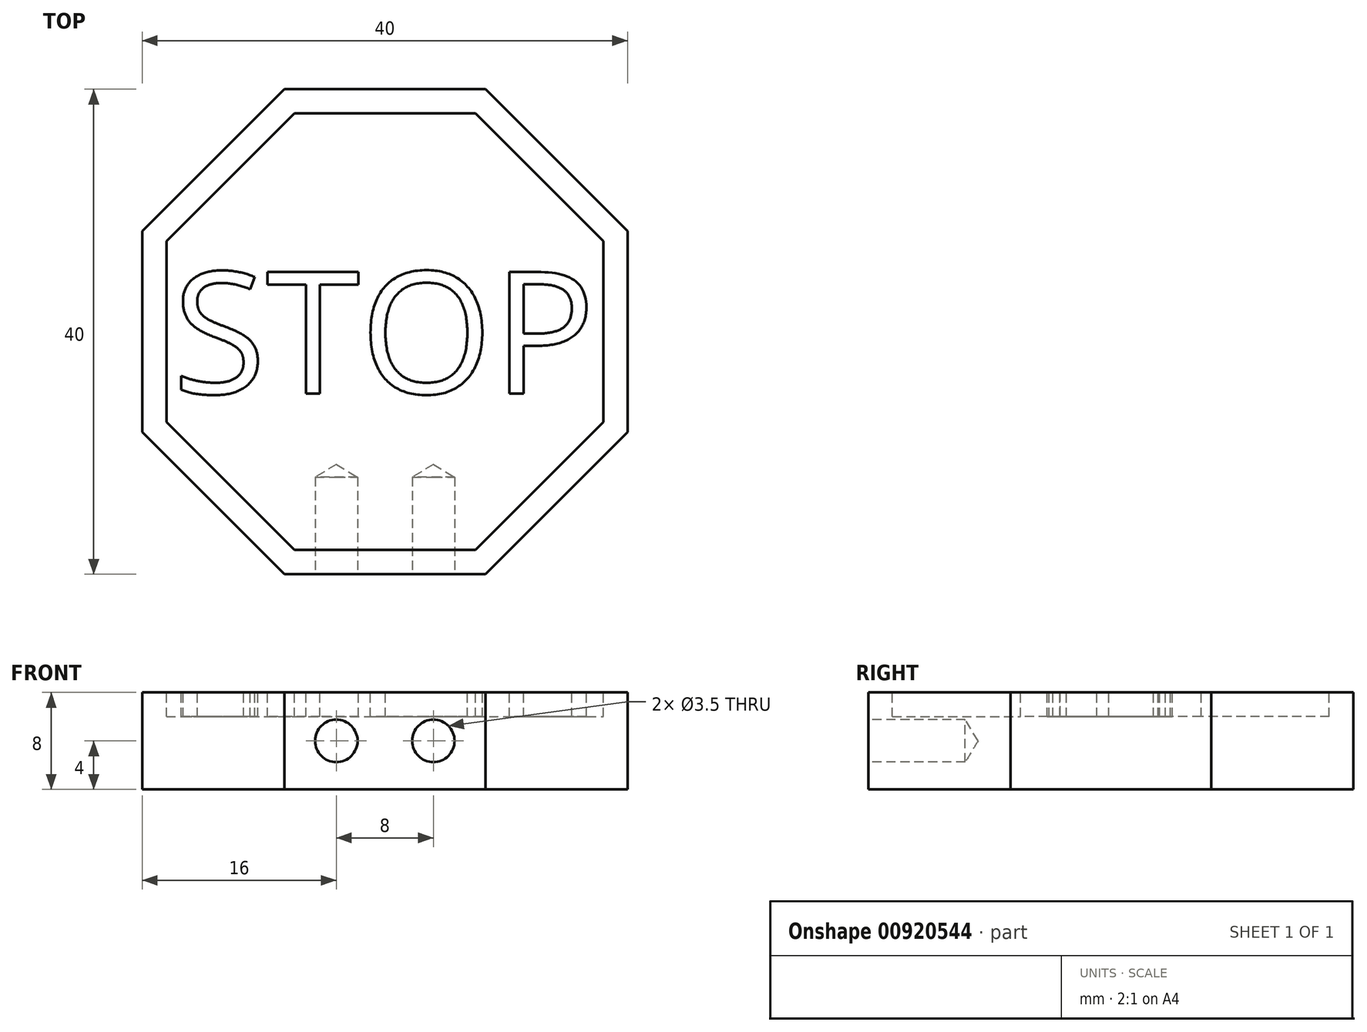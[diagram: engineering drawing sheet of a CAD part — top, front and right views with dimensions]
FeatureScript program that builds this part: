
annotation { "Feature Type Name" : "Feature", "Feature Type Description" : "" }
export const myFeature = defineFeature(function(context is Context, id is Id, definition is map)
    precondition{}
    {
        {
            var Q0;
            Q0=qCreatedBy(makeId("Top.planeOp"),FACE);
            var sketch = newSketch(context, id + "F0", { "sketchPlane" : qUnion([Q0])});
            skCircle(sketch, "E0.cCircle", {"center": v(0, 0) * mm, "radius": 20 * mm, "construction": true});
            skLineSegment(sketch, "E0.0", {"start": v(20, 8.28) * mm, "end": v(20, -8.28) * mm});
            skLineSegment(sketch, "E0.1", {"start": v(20, -8.28) * mm, "end": v(8.28, -20) * mm});
            skLineSegment(sketch, "E0.2", {"start": v(8.28, -20) * mm, "end": v(-8.28, -20) * mm});
            skLineSegment(sketch, "E0.3", {"start": v(-8.28, -20) * mm, "end": v(-20, -8.28) * mm});
            skLineSegment(sketch, "E0.4", {"start": v(-20, -8.28) * mm, "end": v(-20, 8.28) * mm});
            skLineSegment(sketch, "E0.5", {"start": v(-20, 8.28) * mm, "end": v(-8.28, 20) * mm});
            skLineSegment(sketch, "E0.6", {"start": v(-8.28, 20) * mm, "end": v(8.28, 20) * mm});
            skLineSegment(sketch, "E0.7", {"start": v(8.28, 20) * mm, "end": v(20, 8.28) * mm});
            skPoint(sketch, "E0.0.midPoint", {"position": v(20, 0) * mm});
            skSolve(sketch);
        }
        {
            var Q0;
            Q0=makeQuery(id+"F0.imprint","IMPRINT",FACE,{"disambiguationData":[TD([[makeQuery(id+"F0.imprint","IMPRINT",EDGE,{"derivedFrom":sQuery(id+"F0.wireOp",EDGE,"E0.0")}),-1.0]])]});
            extrude(context, id + "F1", {"entities" : qUnion([Q0]), "depth" : 8 * mm, "offsetDistance" : 25 * mm});
        }
        {
            var Q0;
            Q0=makeQuery(id+"F1.opExtrude","CAP_FACE",FACE,{"disambiguationData":[OSD([sQuery(id+"F0.wireOp",EDGE,"E0.0"),sQuery(id+"F0.wireOp",EDGE,"E0.1"),sQuery(id+"F0.wireOp",EDGE,"E0.2"),sQuery(id+"F0.wireOp",EDGE,"E0.3"),sQuery(id+"F0.wireOp",EDGE,"E0.4"),sQuery(id+"F0.wireOp",EDGE,"E0.5"),sQuery(id+"F0.wireOp",EDGE,"E0.6"),sQuery(id+"F0.wireOp",EDGE,"E0.7")])],"isStart":false});
            var sketch = newSketch(context, id + "F2", { "sketchPlane" : qUnion([Q0])});
            skCircle(sketch, "E1.cCircle", {"center": v(0, 0) * mm, "radius": 18 * mm, "construction": true});
            skLineSegment(sketch, "E1.0", {"start": v(18, 7.46) * mm, "end": v(18, -7.46) * mm});
            skLineSegment(sketch, "E1.1", {"start": v(18, -7.46) * mm, "end": v(7.46, -18) * mm});
            skLineSegment(sketch, "E1.2", {"start": v(7.46, -18) * mm, "end": v(-7.46, -18) * mm});
            skLineSegment(sketch, "E1.3", {"start": v(-7.46, -18) * mm, "end": v(-18, -7.46) * mm});
            skLineSegment(sketch, "E1.4", {"start": v(-18, -7.46) * mm, "end": v(-18, 7.46) * mm});
            skLineSegment(sketch, "E1.5", {"start": v(-18, 7.46) * mm, "end": v(-7.46, 18) * mm});
            skLineSegment(sketch, "E1.6", {"start": v(-7.46, 18) * mm, "end": v(7.46, 18) * mm});
            skLineSegment(sketch, "E1.7", {"start": v(7.46, 18) * mm, "end": v(18, 7.46) * mm});
            skPoint(sketch, "E1.0.midPoint", {"position": v(18, 0) * mm});
            skText(sketch, "E2", { "text": "STOP", "fontName": "OpenSans-Regular.ttf"});
            const initialGuessF2  = {"E2": [-0.0175, -0.0051, 1, 0, 0.0101]};
            skSetInitialGuess(sketch, initialGuessF2);
            skSolve(sketch);
        }
        {
            var Q0;
            Q0=makeQuery(id+"F2.imprint","IMPRINT",FACE,{"disambiguationData":[TD([[makeQuery(id+"F2.imprint","IMPRINT",EDGE,{"derivedFrom":sQuery(id+"F2.wireOp",EDGE,"E1.0")}),-1.0]])]});
            var Q1;
            Q1=makeQuery(id+"F2.imprint","IMPRINT",FACE,{"disambiguationData":[TD([[makeQuery(id+"F2.imprint","IMPRINT",EDGE,{"derivedFrom":sQuery(id+"F2.wireOp",EDGE,"E2.sketch_text.stroke-41")}),1.0]])]});
            var Q2;
            Q2=makeQuery(id+"F2.imprint","IMPRINT",FACE,{"disambiguationData":[TD([[makeQuery(id+"F2.imprint","IMPRINT",EDGE,{"derivedFrom":sQuery(id+"F2.wireOp",EDGE,"E2.sketch_text.stroke-57")}),1.0]])]});
            extrude(context, id + "F3", {"entities" : qUnion([Q0, Q1, Q2]), "operationType" : NewBodyOperationType.REMOVE, "oppositeDirection" : true, "depth" : 2 * mm, "offsetDistance" : 25 * mm});
        }
        {
            var Q0;
            Q0=makeQuery(id+"F1.opExtrude","SWEPT_FACE",FACE,{"disambiguationData":[OSD([sQuery(id+"F0.wireOp",EDGE,"E0.2")])]});
            var sketch = newSketch(context, id + "F4", { "sketchPlane" : qUnion([Q0])});
            skPoint(sketch, "E3", {"position": v(-4, 4) * mm});
            skPoint(sketch, "E4.MirrorP", {"position": v(4, 4) * mm});
            skSolve(sketch);
        }
        {
            var Q0;
            Q0=sQuery(id+"F4.wireOp",VERTEX,"E3");
            var Q1;
            Q1=sQuery(id+"F4.wireOp",VERTEX,"E4.MirrorP");
            var Q2;
            Q2=makeQuery(id+"F1.opExtrude","SWEPT_BODY",BODY,{"disambiguationData":[OSD([sQuery(id+"F0.wireOp",EDGE,"E0.0"),sQuery(id+"F0.wireOp",EDGE,"E0.1"),sQuery(id+"F0.wireOp",EDGE,"E0.2"),sQuery(id+"F0.wireOp",EDGE,"E0.3"),sQuery(id+"F0.wireOp",EDGE,"E0.4"),sQuery(id+"F0.wireOp",EDGE,"E0.5"),sQuery(id+"F0.wireOp",EDGE,"E0.6"),sQuery(id+"F0.wireOp",EDGE,"E0.7")])]});
            hole(context, id + "F5", {"style" : HoleStyle.SIMPLE, "endStyle" : HoleEndStyle.BLIND, "holeDiameter" : 3.5 * mm, "majorDiameter" : 5 * mm, "holeDepth" : 8 * mm, "isTappedThrough" : true, "tappedDepth" : 12 * mm, "tapClearance" : 3, "locations" : qUnion([Q0, Q1]), "scope" : qUnion([Q2])});
        }
    });
